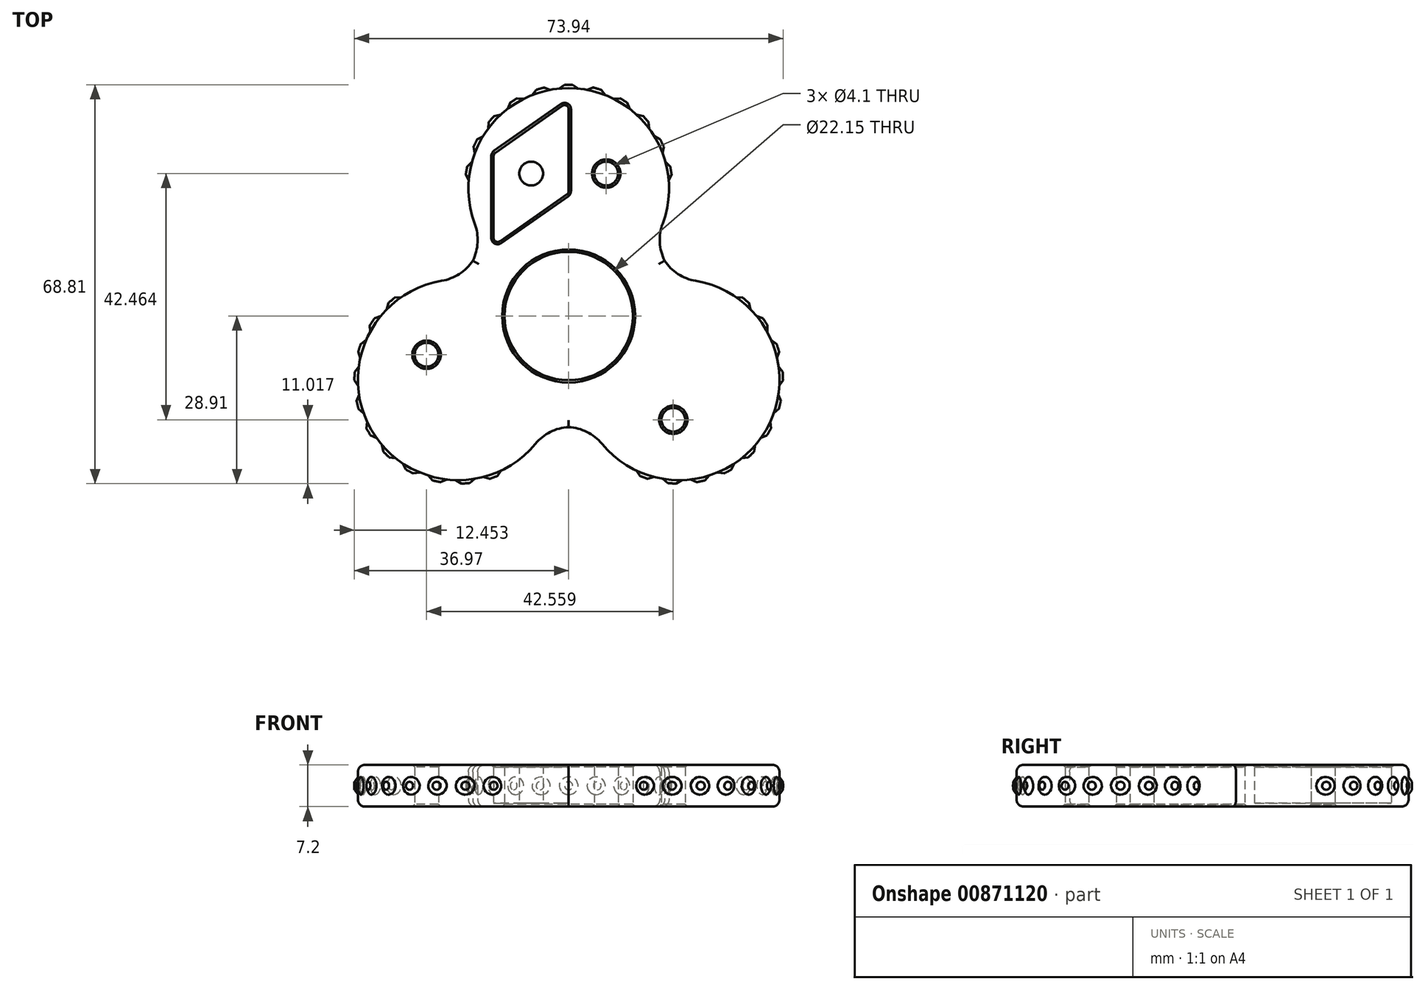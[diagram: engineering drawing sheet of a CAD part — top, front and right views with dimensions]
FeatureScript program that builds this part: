
annotation { "Feature Type Name" : "Feature", "Feature Type Description" : "" }
export const myFeature = defineFeature(function(context is Context, id is Id, definition is map)
    precondition{}
    {
        {
            var Q0;
            Q0=qCreatedBy(makeId("Top.planeOp"),FACE);
            var sketch = newSketch(context, id + "F0", { "sketchPlane" : qUnion([Q0])});
            skCircle(sketch, "E0", {"center": v(0, 0) * mm, "radius": 11.07 * mm});
            skCircle(sketch, "E1", {"center": v(0, 0) * mm, "radius": 26.5 * mm, "construction": true});
            skArc(sketch, "E2", {"start": v(-13.1, 23.03) * mm, "mid": v(-13.03, 22.75) * mm, "end": v(-12.95, 22.47) * mm, "construction": true});
            skLineSegment(sketch, "E3", {"start": v(0, 43.45) * mm, "end": v(0, 0) * mm});
            skLineSegment(sketch, "E4", {"start": v(0, 37) * mm, "end": v(12.95, 27.94) * mm});
            skLineSegment(sketch, "E5", {"start": v(12.95, 27.94) * mm, "end": v(12.95, 12.13) * mm});
            skLineSegment(sketch, "E6", {"start": v(12.95, 12.13) * mm, "end": v(0, 21.2) * mm});
            skLineSegment(sketch, "E7.MirrorCS", {"start": v(0, 37) * mm, "end": v(-12.95, 27.94) * mm});
            skLineSegment(sketch, "E8.MirrorCS", {"start": v(-12.95, 27.94) * mm, "end": v(-12.95, 12.13) * mm});
            skLineSegment(sketch, "E9.MirrorCS", {"start": v(-12.95, 12.13) * mm, "end": v(0, 21.2) * mm});
            skLineSegment(sketch, "E10.1.0", {"start": v(-32.1, -18.57) * mm, "end": v(-17.76, -25.25) * mm});
            skLineSegment(sketch, "E10.1.1", {"start": v(-17.76, -25.25) * mm, "end": v(-4.07, -17.35) * mm});
            skLineSegment(sketch, "E10.1.2", {"start": v(-4.07, -17.35) * mm, "end": v(-18.4, -10.67) * mm});
            skLineSegment(sketch, "E10.1.3", {"start": v(-17.02, 5.08) * mm, "end": v(-18.4, -10.67) * mm});
            skLineSegment(sketch, "E10.1.4", {"start": v(-30.71, -2.82) * mm, "end": v(-17.02, 5.08) * mm});
            skLineSegment(sketch, "E10.1.5", {"start": v(-32.1, -18.57) * mm, "end": v(-30.71, -2.82) * mm});
            skLineSegment(sketch, "E10.2.0", {"start": v(32.1, -18.57) * mm, "end": v(30.71, -2.82) * mm});
            skLineSegment(sketch, "E10.2.1", {"start": v(30.71, -2.82) * mm, "end": v(17.02, 5.08) * mm});
            skLineSegment(sketch, "E10.2.2", {"start": v(17.02, 5.08) * mm, "end": v(18.4, -10.67) * mm});
            skLineSegment(sketch, "E10.2.3", {"start": v(4.07, -17.35) * mm, "end": v(18.4, -10.67) * mm});
            skLineSegment(sketch, "E10.2.4", {"start": v(17.76, -25.25) * mm, "end": v(4.07, -17.35) * mm});
            skLineSegment(sketch, "E10.2.5", {"start": v(32.1, -18.57) * mm, "end": v(17.76, -25.25) * mm});
            skPoint(sketch, "E10.center", {"position": v(0, -0.05) * mm});
            skArc(sketch, "E11.trimOffspring", {"start": v(12.95, 22.47) * mm, "mid": v(13, 22.77) * mm, "end": v(13.05, 23.06) * mm, "construction": true});
            skCircle(sketch, "E12", {"center": v(0, 22) * mm, "radius": 17.3 * mm});
            skCircle(sketch, "E13.1.0", {"center": v(-19.05, -11) * mm, "radius": 17.3 * mm});
            skCircle(sketch, "E13.2.0", {"center": v(19.05, -11) * mm, "radius": 17.3 * mm});
            skLineSegment(sketch, "E14", {"start": v(-17.02, 5.08) * mm, "end": v(-12.95, 12.13) * mm});
            skLineSegment(sketch, "E15", {"start": v(12.95, 12.13) * mm, "end": v(17.02, 5.08) * mm});
            skLineSegment(sketch, "E16", {"start": v(4.07, -17.35) * mm, "end": v(-4.07, -17.35) * mm});
            skLineSegment(sketch, "E17", {"start": v(-7.18, -19.14) * mm, "end": v(7.18, -19.14) * mm});
            skLineSegment(sketch, "E18.1.0", {"start": v(20.13, 3.3) * mm, "end": v(12.96, 15.73) * mm});
            skLineSegment(sketch, "E18.2.0", {"start": v(-12.96, 15.73) * mm, "end": v(-20.13, 3.3) * mm});
            skPoint(sketch, "E18.center", {"position": v(0, -0.03) * mm});
            skLineSegment(sketch, "E19", {"start": v(-12.95, 27.94) * mm, "end": v(0, 21.2) * mm, "construction": true});
            skLineSegment(sketch, "E20", {"start": v(-12.95, 12.13) * mm, "end": v(0, 37) * mm, "construction": true});
            skCircle(sketch, "E21", {"center": v(-6.47, 24.57) * mm, "radius": 2.05 * mm});
            skCircle(sketch, "E22.MirrorC", {"center": v(6.47, 24.57) * mm, "radius": 2.05 * mm});
            skCircle(sketch, "E23.1.0", {"center": v(-24.52, -6.68) * mm, "radius": 2.05 * mm});
            skCircle(sketch, "E23.1.1", {"center": v(-18.04, -17.9) * mm, "radius": 2.05 * mm});
            skCircle(sketch, "E23.2.0", {"center": v(18.04, -17.9) * mm, "radius": 2.05 * mm});
            skCircle(sketch, "E23.2.1", {"center": v(24.52, -6.68) * mm, "radius": 2.05 * mm});
            skSolve(sketch);
        }
        {
            var Q0;
            {var subQ1=sQuery(id+"F0.wireOp",EDGE,"E7.MirrorCS");Q0=makeQuery(id+"F0.imprint","IMPRINT",FACE,{"disambiguationData":[TD([[makeQuery(id+"F0.imprint","IMPRINT",EDGE,{"derivedFrom":subQ1}),-1.0]])]});}
            var Q1;
            {var subQ0=sQuery(id+"F0.wireOp",EDGE,"E4");Q1=makeQuery(id+"F0.imprint","IMPRINT",FACE,{"disambiguationData":[TD([[makeQuery(id+"F0.imprint","IMPRINT",EDGE,{"derivedFrom":subQ0}),1.0]])]});}
            var Q2;
            {var subQ5=sQuery(id+"F0.wireOp",EDGE,"E6");Q2=makeQuery(id+"F0.imprint","IMPRINT",FACE,{"disambiguationData":[TD([[makeQuery(id+"F0.imprint","IMPRINT",EDGE,{"derivedFrom":subQ5}),1.0]])]});}
            var Q3;
            {var subQ0=sQuery(id+"F0.wireOp",EDGE,"E9.MirrorCS");Q3=makeQuery(id+"F0.imprint","IMPRINT",FACE,{"disambiguationData":[TD([[makeQuery(id+"F0.imprint","IMPRINT",EDGE,{"derivedFrom":subQ0}),-1.0]])]});}
            var Q4;
            {var subQ0=sQuery(id+"F0.wireOp",EDGE,"E12");var subQ1=sQuery(id+"F0.wireOp",EDGE,"E0");var subQ2=makeQuery(id+"F0.imprint","INTERSECT",VERTEX,{"disambiguationData":[OD(1.0)],"derivedFrom":[subQ1,subQ0]});Q4=makeQuery(id+"F0.imprint","IMPRINT",FACE,{"disambiguationData":[TD([[makeQuery(id+"F0.imprint","IMPRINT",EDGE,{"disambiguationData":[TD([[subQ2,-1.0]])],"derivedFrom":subQ1}),-1.0]])]});}
            var Q5;
            {var subQ1=sQuery(id+"F0.wireOp",EDGE,"E10.1.2");Q5=makeQuery(id+"F0.imprint","IMPRINT",FACE,{"disambiguationData":[TD([[makeQuery(id+"F0.imprint","IMPRINT",EDGE,{"derivedFrom":subQ1}),-1.0]])]});}
            var Q6;
            {var subQ0=sQuery(id+"F0.wireOp",EDGE,"E13.1.0");var subQ1=sQuery(id+"F0.wireOp",EDGE,"E0");var subQ2=makeQuery(id+"F0.imprint","INTERSECT",VERTEX,{"disambiguationData":[OD(1.0)],"derivedFrom":[subQ1,subQ0]});Q6=makeQuery(id+"F0.imprint","IMPRINT",FACE,{"disambiguationData":[TD([[makeQuery(id+"F0.imprint","IMPRINT",EDGE,{"disambiguationData":[TD([[subQ2,-1.0]])],"derivedFrom":subQ1}),-1.0]])]});}
            var Q7;
            {var subQ9=sQuery(id+"F0.wireOp",EDGE,"E10.2.2");Q7=makeQuery(id+"F0.imprint","IMPRINT",FACE,{"disambiguationData":[TD([[makeQuery(id+"F0.imprint","IMPRINT",EDGE,{"derivedFrom":subQ9}),-1.0]])]});}
            var Q8;
            {var subQ0=sQuery(id+"F0.wireOp",EDGE,"E12");var subQ1=sQuery(id+"F0.wireOp",EDGE,"E0");var subQ2=makeQuery(id+"F0.imprint","INTERSECT",VERTEX,{"disambiguationData":[OD(0.0)],"derivedFrom":[subQ1,subQ0]});Q8=makeQuery(id+"F0.imprint","IMPRINT",FACE,{"disambiguationData":[TD([[makeQuery(id+"F0.imprint","IMPRINT",EDGE,{"disambiguationData":[TD([[subQ2,1.0]])],"derivedFrom":subQ1}),-1.0]])]});}
            var Q9;
            {var subQ6=sQuery(id+"F0.wireOp",EDGE,"E10.2.0");Q9=makeQuery(id+"F0.imprint","IMPRINT",FACE,{"disambiguationData":[TD([[makeQuery(id+"F0.imprint","IMPRINT",EDGE,{"derivedFrom":subQ6}),-1.0]])]});}
            var Q10;
            {var subQ7=sQuery(id+"F0.wireOp",EDGE,"E10.1.0");Q10=makeQuery(id+"F0.imprint","IMPRINT",FACE,{"disambiguationData":[TD([[makeQuery(id+"F0.imprint","IMPRINT",EDGE,{"derivedFrom":subQ7}),-1.0]])]});}
            var Q11;
            {var subQ0=sQuery(id+"F0.wireOp",EDGE,"E18.2.0");var subQ1=sQuery(id+"F0.wireOp",EDGE,"E12");var subQ2=makeQuery(id+"F0.imprint","INTERSECT",VERTEX,{"derivedFrom":[subQ1,subQ0]});Q11=makeQuery(id+"F0.imprint","IMPRINT",FACE,{"disambiguationData":[TD([[makeQuery(id+"F0.imprint","IMPRINT",EDGE,{"disambiguationData":[TD([[subQ2,-1.0]])],"derivedFrom":subQ1}),-1.0]])]});}
            var Q12;
            {var subQ0=sQuery(id+"F0.wireOp",EDGE,"E17");var subQ1=sQuery(id+"F0.wireOp",EDGE,"E13.1.0");var subQ2=makeQuery(id+"F0.imprint","INTERSECT",VERTEX,{"derivedFrom":[subQ1,subQ0]});Q12=makeQuery(id+"F0.imprint","IMPRINT",FACE,{"disambiguationData":[TD([[makeQuery(id+"F0.imprint","IMPRINT",EDGE,{"disambiguationData":[TD([[subQ2,-1.0]])],"derivedFrom":subQ1}),-1.0]])]});}
            var Q13;
            {var subQ3=sQuery(id+"F0.wireOp",EDGE,"E18.2.0");var subQ5=sQuery(id+"F0.wireOp",EDGE,"E12");var subQ7=makeQuery(id+"F0.imprint","INTERSECT",VERTEX,{"derivedFrom":[subQ5,subQ3]});Q13=makeQuery(id+"F0.imprint","IMPRINT",FACE,{"disambiguationData":[TD([[makeQuery(id+"F0.imprint","IMPRINT",EDGE,{"disambiguationData":[TD([[subQ7,-1.0]])],"derivedFrom":subQ5}),1.0]])]});}
            var Q14;
            {var subQ3=sQuery(id+"F0.wireOp",EDGE,"E18.2.0");var subQ5=sQuery(id+"F0.wireOp",EDGE,"E13.1.0");var subQ7=makeQuery(id+"F0.imprint","INTERSECT",VERTEX,{"derivedFrom":[subQ5,subQ3]});Q14=makeQuery(id+"F0.imprint","IMPRINT",FACE,{"disambiguationData":[TD([[makeQuery(id+"F0.imprint","IMPRINT",EDGE,{"disambiguationData":[TD([[subQ7,1.0]])],"derivedFrom":subQ5}),1.0]])]});}
            var Q15;
            {var subQ3=sQuery(id+"F0.wireOp",EDGE,"E17");var subQ5=sQuery(id+"F0.wireOp",EDGE,"E13.1.0");var subQ6=makeQuery(id+"F0.imprint","INTERSECT",VERTEX,{"derivedFrom":[subQ5,subQ3]});Q15=makeQuery(id+"F0.imprint","IMPRINT",FACE,{"disambiguationData":[TD([[makeQuery(id+"F0.imprint","IMPRINT",EDGE,{"disambiguationData":[TD([[subQ6,-1.0]])],"derivedFrom":subQ5}),1.0]])]});}
            var Q16;
            {var subQ3=sQuery(id+"F0.wireOp",EDGE,"E17");var subQ5=sQuery(id+"F0.wireOp",EDGE,"E13.2.0");var subQ6=makeQuery(id+"F0.imprint","INTERSECT",VERTEX,{"derivedFrom":[subQ5,subQ3]});Q16=makeQuery(id+"F0.imprint","IMPRINT",FACE,{"disambiguationData":[TD([[makeQuery(id+"F0.imprint","IMPRINT",EDGE,{"disambiguationData":[TD([[subQ6,1.0]])],"derivedFrom":subQ5}),1.0]])]});}
            var Q17;
            {var subQ3=sQuery(id+"F0.wireOp",EDGE,"E18.1.0");var subQ5=sQuery(id+"F0.wireOp",EDGE,"E12");var subQ7=makeQuery(id+"F0.imprint","INTERSECT",VERTEX,{"derivedFrom":[subQ5,subQ3]});Q17=makeQuery(id+"F0.imprint","IMPRINT",FACE,{"disambiguationData":[TD([[makeQuery(id+"F0.imprint","IMPRINT",EDGE,{"disambiguationData":[TD([[subQ7,1.0]])],"derivedFrom":subQ5}),1.0]])]});}
            var Q18;
            {var subQ3=sQuery(id+"F0.wireOp",EDGE,"E18.1.0");var subQ5=sQuery(id+"F0.wireOp",EDGE,"E13.2.0");var subQ6=makeQuery(id+"F0.imprint","INTERSECT",VERTEX,{"derivedFrom":[subQ5,subQ3]});Q18=makeQuery(id+"F0.imprint","IMPRINT",FACE,{"disambiguationData":[TD([[makeQuery(id+"F0.imprint","IMPRINT",EDGE,{"disambiguationData":[TD([[subQ6,-1.0]])],"derivedFrom":subQ5}),1.0]])]});}
            var Q19;
            {var subQ0=sQuery(id+"F0.wireOp",EDGE,"E18.1.0");var subQ1=sQuery(id+"F0.wireOp",EDGE,"E12");var subQ2=makeQuery(id+"F0.imprint","INTERSECT",VERTEX,{"derivedFrom":[subQ1,subQ0]});Q19=makeQuery(id+"F0.imprint","IMPRINT",FACE,{"disambiguationData":[TD([[makeQuery(id+"F0.imprint","IMPRINT",EDGE,{"disambiguationData":[TD([[subQ2,1.0]])],"derivedFrom":subQ1}),-1.0]])]});}
            var Q20;
            Q20=makeQuery(id+"F0.imprint","IMPRINT",FACE,{"disambiguationData":[TD([[makeQuery(id+"F0.imprint","IMPRINT",EDGE,{"derivedFrom":sQuery(id+"F0.wireOp",EDGE,"E23.1.0")}),-1.0]])]});
            var Q21;
            Q21=makeQuery(id+"F0.imprint","IMPRINT",FACE,{"disambiguationData":[TD([[makeQuery(id+"F0.imprint","IMPRINT",EDGE,{"derivedFrom":sQuery(id+"F0.wireOp",EDGE,"E23.1.1")}),1.0]])]});
            var Q22;
            Q22=makeQuery(id+"F0.imprint","IMPRINT",FACE,{"disambiguationData":[TD([[makeQuery(id+"F0.imprint","IMPRINT",EDGE,{"derivedFrom":sQuery(id+"F0.wireOp",EDGE,"E23.2.1")}),1.0]])]});
            var Q23;
            Q23=makeQuery(id+"F0.imprint","IMPRINT",FACE,{"disambiguationData":[TD([[makeQuery(id+"F0.imprint","IMPRINT",EDGE,{"derivedFrom":sQuery(id+"F0.wireOp",EDGE,"E23.2.0")}),-1.0]])]});
            var Q24;
            Q24=makeQuery(id+"F0.imprint","IMPRINT",FACE,{"disambiguationData":[TD([[makeQuery(id+"F0.imprint","IMPRINT",EDGE,{"derivedFrom":sQuery(id+"F0.wireOp",EDGE,"E22.MirrorC")}),-1.0]])]});
            var Q25;
            Q25=makeQuery(id+"F0.imprint","IMPRINT",FACE,{"disambiguationData":[TD([[makeQuery(id+"F0.imprint","IMPRINT",EDGE,{"derivedFrom":sQuery(id+"F0.wireOp",EDGE,"E21")}),1.0]])]});
            extrude(context, id + "F1", {"entities" : qUnion([Q0, Q1, Q2, Q3, Q4, Q5, Q6, Q7, Q8, Q9, Q10, Q11, Q12, Q13, Q14, Q15, Q16, Q17, Q18, Q19, Q20, Q21, Q22, Q23, Q24, Q25]), "depth" : 7.2 * mm, "offsetDistance" : 25 * mm});
        }
        {
            var Q0;
            {var subQ1=sQuery(id+"F0.wireOp",EDGE,"E4");Q0=makeQuery(id+"F0.imprint","IMPRINT",FACE,{"disambiguationData":[TD([[makeQuery(id+"F0.imprint","IMPRINT",EDGE,{"derivedFrom":subQ1}),-1.0]])]});}
            var Q1;
            {var subQ3=sQuery(id+"F0.wireOp",EDGE,"E7.MirrorCS");Q1=makeQuery(id+"F0.imprint","IMPRINT",FACE,{"disambiguationData":[TD([[makeQuery(id+"F0.imprint","IMPRINT",EDGE,{"derivedFrom":subQ3}),1.0]])]});}
            var Q2;
            {var subQ3=sQuery(id+"F0.wireOp",EDGE,"E10.2.0");Q2=makeQuery(id+"F0.imprint","IMPRINT",FACE,{"disambiguationData":[TD([[makeQuery(id+"F0.imprint","IMPRINT",EDGE,{"derivedFrom":subQ3}),1.0]])]});}
            var Q3;
            {var subQ3=sQuery(id+"F0.wireOp",EDGE,"E10.1.0");Q3=makeQuery(id+"F0.imprint","IMPRINT",FACE,{"disambiguationData":[TD([[makeQuery(id+"F0.imprint","IMPRINT",EDGE,{"derivedFrom":subQ3}),1.0]])]});}
            extrude(context, id + "F2", {"entities" : qUnion([Q0, Q1, Q2, Q3]), "operationType" : NewBodyOperationType.ADD, "depth" : 0.6 * mm, "offsetDistance" : 25 * mm});
        }
        {
            var Q0;
            Q0=makeQuery(id+"F1.opExtrude","SWEPT_EDGE",EDGE,{"disambiguationData":[OSD([sQuery(id+"F0.wireOp",EDGE,"E12"),sQuery(id+"F0.wireOp",EDGE,"Zo6cloxw-RQWd-VoTV-Hmrh-WUM4IXPVoAln")])]});
            var Q1;
            Q1=makeQuery(id+"F1.opExtrude","SWEPT_EDGE",EDGE,{"disambiguationData":[OSD([sQuery(id+"F0.wireOp",EDGE,"E13.1.0"),sQuery(id+"F0.wireOp",EDGE,"Zo6cloxw-RQWd-VoTV-Hmrh-WUM4IXPVoAln")])]});
            var Q2;
            Q2=makeQuery(id+"F1.opExtrude","SWEPT_EDGE",EDGE,{"disambiguationData":[OSD([sQuery(id+"F0.wireOp",EDGE,"E13.2.0"),sQuery(id+"F0.wireOp",EDGE,"qCIH2ttQ-GXot-xXQ0-Qejf-B46ZgPa41a3F")])]});
            var Q3;
            Q3=makeQuery(id+"F1.opExtrude","SWEPT_EDGE",EDGE,{"disambiguationData":[OSD([sQuery(id+"F0.wireOp",EDGE,"E12"),sQuery(id+"F0.wireOp",EDGE,"qCIH2ttQ-GXot-xXQ0-Qejf-B46ZgPa41a3F")])]});
            var Q4;
            Q4=makeQuery(id+"F1.opExtrude","SWEPT_EDGE",EDGE,{"disambiguationData":[OSD([sQuery(id+"F0.wireOp",EDGE,"E13.2.0"),sQuery(id+"F0.wireOp",EDGE,"L0YcY93C-S2HS-15lv-KyWX-i7wwrRtpjOze")])]});
            var Q5;
            Q5=makeQuery(id+"F1.opExtrude","SWEPT_EDGE",EDGE,{"disambiguationData":[OSD([sQuery(id+"F0.wireOp",EDGE,"E13.1.0"),sQuery(id+"F0.wireOp",EDGE,"L0YcY93C-S2HS-15lv-KyWX-i7wwrRtpjOze")])]});
            fillet(context, id + "F3", {"entities" : qUnion([Q0, Q1, Q2, Q3, Q4, Q5]), "radius" : 8 * mm, "tangentPropagation" : true, "allowEdgeOverflow" : false});
        }
        {
            var Q0;
            Q0=makeQuery(id+"F1.opExtrude","CAP_EDGE",EDGE,{"disambiguationData":[OSD([sQuery(id+"F0.wireOp",EDGE,"E13.2.0")])],"isStart":true});
            var Q1;
            Q1=makeQuery(id+"F1.opExtrude","CAP_EDGE",EDGE,{"disambiguationData":[OSD([sQuery(id+"F0.wireOp",EDGE,"E13.1.0")])],"isStart":true});
            var Q2;
            Q2=makeQuery(id+"F1.opExtrude","CAP_EDGE",EDGE,{"disambiguationData":[OSD([sQuery(id+"F0.wireOp",EDGE,"E12")])],"isStart":true});
            var Q3;
            Q3=makeQuery(id+"F1.opExtrude","CAP_EDGE",EDGE,{"disambiguationData":[OSD([sQuery(id+"F0.wireOp",EDGE,"E12")])],"isStart":false});
            var Q4;
            Q4=makeQuery(id+"F1.opExtrude","CAP_EDGE",EDGE,{"disambiguationData":[OSD([sQuery(id+"F0.wireOp",EDGE,"E13.2.0")])],"isStart":false});
            var Q5;
            Q5=makeQuery(id+"F1.opExtrude","CAP_EDGE",EDGE,{"disambiguationData":[OSD([sQuery(id+"F0.wireOp",EDGE,"E13.1.0")])],"isStart":false});
            fillet(context, id + "F4", {"entities" : qUnion([Q0, Q1, Q2, Q3, Q4, Q5]), "radius" : 1.2 * mm, "tangentPropagation" : true, "allowEdgeOverflow" : false});
        }
        {
            var Q0;
            Q0=makeQuery(id+"F1.opExtrude","SWEPT_EDGE",EDGE,{"disambiguationData":[OSD([sQuery(id+"F0.wireOp",EDGE,"E10.1.0"),sQuery(id+"F0.wireOp",EDGE,"E10.1.5")])]});
            var Q1;
            Q1=makeQuery(id+"F1.opExtrude","SWEPT_EDGE",EDGE,{"disambiguationData":[OSD([sQuery(id+"F0.wireOp",EDGE,"E10.1.1"),sQuery(id+"F0.wireOp",EDGE,"E10.1.2"),sQuery(id+"F0.wireOp",EDGE,"L0YcY93C-S2HS-15lv-KyWX-i7wwrRtpjOze")])]});
            var Q2;
            Q2=makeQuery(id+"F1.opExtrude","SWEPT_EDGE",EDGE,{"disambiguationData":[OSD([sQuery(id+"F0.wireOp",EDGE,"E10.1.3"),sQuery(id+"F0.wireOp",EDGE,"E10.1.4"),sQuery(id+"F0.wireOp",EDGE,"Zo6cloxw-RQWd-VoTV-Hmrh-WUM4IXPVoAln")])]});
            var Q3;
            Q3=makeQuery(id+"F1.opExtrude","SWEPT_EDGE",EDGE,{"disambiguationData":[OSD([sQuery(id+"F0.wireOp",EDGE,"E10.1.0"),sQuery(id+"F0.wireOp",EDGE,"E10.1.1")])]});
            var Q4;
            Q4=makeQuery(id+"F1.opExtrude","SWEPT_EDGE",EDGE,{"disambiguationData":[OSD([sQuery(id+"F0.wireOp",EDGE,"E10.1.4"),sQuery(id+"F0.wireOp",EDGE,"E10.1.5")])]});
            var Q5;
            Q5=makeQuery(id+"F1.opExtrude","SWEPT_EDGE",EDGE,{"disambiguationData":[OSD([sQuery(id+"F0.wireOp",EDGE,"E10.2.3"),sQuery(id+"F0.wireOp",EDGE,"E10.2.4"),sQuery(id+"F0.wireOp",EDGE,"L0YcY93C-S2HS-15lv-KyWX-i7wwrRtpjOze")])]});
            var Q6;
            Q6=makeQuery(id+"F1.opExtrude","SWEPT_EDGE",EDGE,{"disambiguationData":[OSD([sQuery(id+"F0.wireOp",EDGE,"E10.2.4"),sQuery(id+"F0.wireOp",EDGE,"E10.2.5")])]});
            var Q7;
            Q7=makeQuery(id+"F1.opExtrude","SWEPT_EDGE",EDGE,{"disambiguationData":[OSD([sQuery(id+"F0.wireOp",EDGE,"E10.2.0"),sQuery(id+"F0.wireOp",EDGE,"E10.2.5")])]});
            var Q8;
            Q8=makeQuery(id+"F1.opExtrude","SWEPT_EDGE",EDGE,{"disambiguationData":[OSD([sQuery(id+"F0.wireOp",EDGE,"E10.2.0"),sQuery(id+"F0.wireOp",EDGE,"E10.2.1")])]});
            var Q9;
            Q9=makeQuery(id+"F1.opExtrude","SWEPT_EDGE",EDGE,{"disambiguationData":[OSD([sQuery(id+"F0.wireOp",EDGE,"E10.2.1"),sQuery(id+"F0.wireOp",EDGE,"E10.2.2"),sQuery(id+"F0.wireOp",EDGE,"qCIH2ttQ-GXot-xXQ0-Qejf-B46ZgPa41a3F")])]});
            var Q10;
            Q10=makeQuery(id+"F1.opExtrude","SWEPT_EDGE",EDGE,{"disambiguationData":[OSD([sQuery(id+"F0.wireOp",EDGE,"E5"),sQuery(id+"F0.wireOp",EDGE,"E6"),sQuery(id+"F0.wireOp",EDGE,"qCIH2ttQ-GXot-xXQ0-Qejf-B46ZgPa41a3F")])]});
            var Q11;
            Q11=makeQuery(id+"F1.opExtrude","SWEPT_EDGE",EDGE,{"disambiguationData":[OSD([sQuery(id+"F0.wireOp",EDGE,"E8.MirrorCS"),sQuery(id+"F0.wireOp",EDGE,"E9.MirrorCS"),sQuery(id+"F0.wireOp",EDGE,"Zo6cloxw-RQWd-VoTV-Hmrh-WUM4IXPVoAln")])]});
            var Q12;
            Q12=makeQuery(id+"F1.opExtrude","SWEPT_EDGE",EDGE,{"disambiguationData":[OSD([sQuery(id+"F0.wireOp",EDGE,"E4"),sQuery(id+"F0.wireOp",EDGE,"E5")])]});
            var Q13;
            Q13=makeQuery(id+"F1.opExtrude","SWEPT_EDGE",EDGE,{"disambiguationData":[OSD([sQuery(id+"F0.wireOp",EDGE,"E3"),sQuery(id+"F0.wireOp",EDGE,"E4"),sQuery(id+"F0.wireOp",EDGE,"E7.MirrorCS")])]});
            var Q14;
            Q14=makeQuery(id+"F1.opExtrude","SWEPT_EDGE",EDGE,{"disambiguationData":[OSD([sQuery(id+"F0.wireOp",EDGE,"E7.MirrorCS"),sQuery(id+"F0.wireOp",EDGE,"E8.MirrorCS")])]});
            fillet(context, id + "F5", {"entities" : qUnion([Q0, Q1, Q2, Q3, Q4, Q5, Q6, Q7, Q8, Q9, Q10, Q11, Q12, Q13, Q14]), "radius" : 0.7 * mm, "tangentPropagation" : true, "allowEdgeOverflow" : false});
        }
        {
            var Q0;
            Q0=makeQuery(id+"F1.opExtrude","CAP_FACE",FACE,{"disambiguationData":[OSD([sQuery(id+"F0.wireOp",EDGE,"E0"),sQuery(id+"F0.wireOp",EDGE,"E4"),sQuery(id+"F0.wireOp",EDGE,"E5"),sQuery(id+"F0.wireOp",EDGE,"E6"),sQuery(id+"F0.wireOp",EDGE,"E7.MirrorCS"),sQuery(id+"F0.wireOp",EDGE,"E8.MirrorCS"),sQuery(id+"F0.wireOp",EDGE,"E9.MirrorCS"),sQuery(id+"F0.wireOp",EDGE,"E10.1.0"),sQuery(id+"F0.wireOp",EDGE,"E10.1.1"),sQuery(id+"F0.wireOp",EDGE,"E10.1.2"),sQuery(id+"F0.wireOp",EDGE,"E10.1.3"),sQuery(id+"F0.wireOp",EDGE,"E10.1.4"),sQuery(id+"F0.wireOp",EDGE,"E10.1.5"),sQuery(id+"F0.wireOp",EDGE,"E10.2.0"),sQuery(id+"F0.wireOp",EDGE,"E10.2.1"),sQuery(id+"F0.wireOp",EDGE,"E10.2.2"),sQuery(id+"F0.wireOp",EDGE,"E10.2.3"),sQuery(id+"F0.wireOp",EDGE,"E10.2.4"),sQuery(id+"F0.wireOp",EDGE,"E10.2.5"),sQuery(id+"F0.wireOp",EDGE,"E12"),sQuery(id+"F0.wireOp",EDGE,"E13.1.0"),sQuery(id+"F0.wireOp",EDGE,"E13.2.0"),sQuery(id+"F0.wireOp",EDGE,"qCIH2ttQ-GXot-xXQ0-Qejf-B46ZgPa41a3F"),sQuery(id+"F0.wireOp",EDGE,"Zo6cloxw-RQWd-VoTV-Hmrh-WUM4IXPVoAln"),sQuery(id+"F0.wireOp",EDGE,"L0YcY93C-S2HS-15lv-KyWX-i7wwrRtpjOze")])],"isStart":true});
            var Q1;
            Q1=makeQuery(id+"F1.opExtrude","CAP_FACE",FACE,{"disambiguationData":[OSD([sQuery(id+"F0.wireOp",EDGE,"E0"),sQuery(id+"F0.wireOp",EDGE,"E4"),sQuery(id+"F0.wireOp",EDGE,"E5"),sQuery(id+"F0.wireOp",EDGE,"E6"),sQuery(id+"F0.wireOp",EDGE,"E7.MirrorCS"),sQuery(id+"F0.wireOp",EDGE,"E8.MirrorCS"),sQuery(id+"F0.wireOp",EDGE,"E9.MirrorCS"),sQuery(id+"F0.wireOp",EDGE,"E10.1.0"),sQuery(id+"F0.wireOp",EDGE,"E10.1.1"),sQuery(id+"F0.wireOp",EDGE,"E10.1.2"),sQuery(id+"F0.wireOp",EDGE,"E10.1.3"),sQuery(id+"F0.wireOp",EDGE,"E10.1.4"),sQuery(id+"F0.wireOp",EDGE,"E10.1.5"),sQuery(id+"F0.wireOp",EDGE,"E10.2.0"),sQuery(id+"F0.wireOp",EDGE,"E10.2.1"),sQuery(id+"F0.wireOp",EDGE,"E10.2.2"),sQuery(id+"F0.wireOp",EDGE,"E10.2.3"),sQuery(id+"F0.wireOp",EDGE,"E10.2.4"),sQuery(id+"F0.wireOp",EDGE,"E10.2.5"),sQuery(id+"F0.wireOp",EDGE,"E12"),sQuery(id+"F0.wireOp",EDGE,"E13.1.0"),sQuery(id+"F0.wireOp",EDGE,"E13.2.0"),sQuery(id+"F0.wireOp",EDGE,"qCIH2ttQ-GXot-xXQ0-Qejf-B46ZgPa41a3F"),sQuery(id+"F0.wireOp",EDGE,"Zo6cloxw-RQWd-VoTV-Hmrh-WUM4IXPVoAln"),sQuery(id+"F0.wireOp",EDGE,"L0YcY93C-S2HS-15lv-KyWX-i7wwrRtpjOze")])],"isStart":false});
            chamfer(context, id + "F6", {"entities" : qUnion([Q0, Q1]), "width" : 0.4 * mm, "tangentPropagation" : true});
        }
        {
            var Q0;
            {var subQ0=sQuery(id+"F0.wireOp",EDGE,"E12");Q0=makeQuery(id+"F4.opFillet","BLEND_EDGE",EDGE,{"blendedFrom":[makeQuery(id+"F1.opExtrude","CAP_EDGE",EDGE,{"disambiguationData":[OSD([subQ0])],"isStart":true}),makeQuery(id+"F1.opExtrude","SWEPT_FACE",FACE,{"disambiguationData":[OSD([subQ0])]})],"blendedInto":[makeQuery(id+"F1.opExtrude","SWEPT_FACE",FACE,{"disambiguationData":[OSD([subQ0])]})]});}
            cPoint(context, id + "F7", {"entities" : qUnion([Q0]), "parameter" : 0.5});
        }
        {
            var Q0;
            Q0=qCreatedBy(makeId("Front.planeOp"),FACE);
            var Q1;
            Q1=qCreatedBy(id+"F7",VERTEX);
            cPlane(context, id + "F8", {"entities" : qUnion([Q0, Q1]), "cplaneType" : CPlaneType.PLANE_POINT, "offset" : 25 * mm, "width" : 150 * mm, "height" : 150 * mm});
        }
        {
            var Q0;
            Q0=qCreatedBy(id+"F8.planeOp",FACE);
            var sketch = newSketch(context, id + "F9", { "sketchPlane" : qUnion([Q0])});
            skCircle(sketch, "E24", {"center": v(0, 3.6) * mm, "radius": 1.8 * mm});
            skSolve(sketch);
        }
        {
            var Q0;
            Q0=makeQuery(id+"F9.imprint","IMPRINT",FACE,{"disambiguationData":[TD([[makeQuery(id+"F9.imprint","IMPRINT",EDGE,{"derivedFrom":sQuery(id+"F9.wireOp",EDGE,"E24")}),1.0]])]});
            var Q1;
            Q1=sQuery(id+"F9.wireOp",EDGE,"E24");
            extrude(context, id + "F10", {"entities" : qUnion([Q0]), "surfaceEntities" : qUnion([Q1]), "oppositeDirection" : true, "depth" : 0.6 * mm, "offsetDistance" : 25 * mm, "hasSecondDirection" : true, "secondDirectionOppositeDirection" : false, "secondDirectionDepth" : 0.4 * mm});
        }
        {
            var Q0;
            Q0=makeQuery(id+"F10.opExtrude","CAP_EDGE",EDGE,{"disambiguationData":[OSD([sQuery(id+"F9.wireOp",EDGE,"E24")])],"isStart":false});
            chamfer(context, id + "F11", {"entities" : qUnion([Q0]), "chamferType" : ChamferType.TWO_OFFSETS, "width1" : 0.8 * mm, "oppositeDirection" : false, "width2" : 1.1 * mm, "tangentPropagation" : true});
        }
        {
            var Q0;
            Q0=makeQuery(id+"F10.opExtrude","SWEPT_BODY",BODY,{"disambiguationData":[OSD([sQuery(id+"F9.wireOp",EDGE,"E24")])]});
            var Q1;
            Q1=makeQuery(id+"F1.opExtrude","SWEPT_FACE",FACE,{"disambiguationData":[OSD([sQuery(id+"F0.wireOp",EDGE,"E12")])]});
            circularPattern(context, id + "F12", {"entities" : qUnion([Q0]), "axis" : qUnion([Q1]), "angle" : 80 * degree, "instanceCount" : 6, "equalSpace" : true, "isCentered" : true});
        }
        {
            var Q0;
            Q0=makeQuery(id+"F10.opExtrude","SWEPT_BODY",BODY,{"disambiguationData":[OSD([sQuery(id+"F9.wireOp",EDGE,"E24")])]});
            var Q1;
            Q1=makeQuery(id+"F12.opPattern","COPY",BODY,{"derivedFrom":makeQuery(id+"F10.opExtrude","SWEPT_BODY",BODY,{"disambiguationData":[OSD([sQuery(id+"F9.wireOp",EDGE,"E24")])]}),"instanceName":"-8"});
            var Q2;
            Q2=makeQuery(id+"F12.opPattern","COPY",BODY,{"derivedFrom":makeQuery(id+"F10.opExtrude","SWEPT_BODY",BODY,{"disambiguationData":[OSD([sQuery(id+"F9.wireOp",EDGE,"E24")])]}),"instanceName":"-7"});
            var Q3;
            Q3=makeQuery(id+"F12.opPattern","COPY",BODY,{"derivedFrom":makeQuery(id+"F10.opExtrude","SWEPT_BODY",BODY,{"disambiguationData":[OSD([sQuery(id+"F9.wireOp",EDGE,"E24")])]}),"instanceName":"-6"});
            var Q4;
            Q4=makeQuery(id+"F12.opPattern","COPY",BODY,{"derivedFrom":makeQuery(id+"F10.opExtrude","SWEPT_BODY",BODY,{"disambiguationData":[OSD([sQuery(id+"F9.wireOp",EDGE,"E24")])]}),"instanceName":"-5"});
            var Q5;
            Q5=makeQuery(id+"F12.opPattern","COPY",BODY,{"derivedFrom":makeQuery(id+"F10.opExtrude","SWEPT_BODY",BODY,{"disambiguationData":[OSD([sQuery(id+"F9.wireOp",EDGE,"E24")])]}),"instanceName":"-4"});
            var Q6;
            Q6=makeQuery(id+"F12.opPattern","COPY",BODY,{"derivedFrom":makeQuery(id+"F10.opExtrude","SWEPT_BODY",BODY,{"disambiguationData":[OSD([sQuery(id+"F9.wireOp",EDGE,"E24")])]}),"instanceName":"-3"});
            var Q7;
            Q7=makeQuery(id+"F12.opPattern","COPY",BODY,{"derivedFrom":makeQuery(id+"F10.opExtrude","SWEPT_BODY",BODY,{"disambiguationData":[OSD([sQuery(id+"F9.wireOp",EDGE,"E24")])]}),"instanceName":"-2"});
            var Q8;
            Q8=makeQuery(id+"F12.opPattern","COPY",BODY,{"derivedFrom":makeQuery(id+"F10.opExtrude","SWEPT_BODY",BODY,{"disambiguationData":[OSD([sQuery(id+"F9.wireOp",EDGE,"E24")])]}),"instanceName":"-1"});
            var Q9;
            Q9=makeQuery(id+"F12.opPattern","COPY",BODY,{"derivedFrom":makeQuery(id+"F10.opExtrude","SWEPT_BODY",BODY,{"disambiguationData":[OSD([sQuery(id+"F9.wireOp",EDGE,"E24")])]}),"instanceName":"1"});
            var Q10;
            Q10=makeQuery(id+"F12.opPattern","COPY",BODY,{"derivedFrom":makeQuery(id+"F10.opExtrude","SWEPT_BODY",BODY,{"disambiguationData":[OSD([sQuery(id+"F9.wireOp",EDGE,"E24")])]}),"instanceName":"2"});
            var Q11;
            Q11=makeQuery(id+"F12.opPattern","COPY",BODY,{"derivedFrom":makeQuery(id+"F10.opExtrude","SWEPT_BODY",BODY,{"disambiguationData":[OSD([sQuery(id+"F9.wireOp",EDGE,"E24")])]}),"instanceName":"3"});
            var Q12;
            Q12=makeQuery(id+"F12.opPattern","COPY",BODY,{"derivedFrom":makeQuery(id+"F10.opExtrude","SWEPT_BODY",BODY,{"disambiguationData":[OSD([sQuery(id+"F9.wireOp",EDGE,"E24")])]}),"instanceName":"4"});
            var Q13;
            Q13=makeQuery(id+"F12.opPattern","COPY",BODY,{"derivedFrom":makeQuery(id+"F10.opExtrude","SWEPT_BODY",BODY,{"disambiguationData":[OSD([sQuery(id+"F9.wireOp",EDGE,"E24")])]}),"instanceName":"5"});
            var Q14;
            Q14=makeQuery(id+"F12.opPattern","COPY",BODY,{"derivedFrom":makeQuery(id+"F10.opExtrude","SWEPT_BODY",BODY,{"disambiguationData":[OSD([sQuery(id+"F9.wireOp",EDGE,"E24")])]}),"instanceName":"6"});
            var Q15;
            Q15=makeQuery(id+"F12.opPattern","COPY",BODY,{"derivedFrom":makeQuery(id+"F10.opExtrude","SWEPT_BODY",BODY,{"disambiguationData":[OSD([sQuery(id+"F9.wireOp",EDGE,"E24")])]}),"instanceName":"7"});
            var Q16;
            Q16=makeQuery(id+"F12.opPattern","COPY",BODY,{"derivedFrom":makeQuery(id+"F10.opExtrude","SWEPT_BODY",BODY,{"disambiguationData":[OSD([sQuery(id+"F9.wireOp",EDGE,"E24")])]}),"instanceName":"8"});
            var Q17;
            Q17=makeQuery(id+"F1.opExtrude","SWEPT_FACE",FACE,{"disambiguationData":[OSD([sQuery(id+"F0.wireOp",EDGE,"E0")])]});
            circularPattern(context, id + "F13", {"operationType" : NewBodyOperationType.ADD, "entities" : qUnion([Q0, Q1, Q2, Q3, Q4, Q5, Q6, Q7, Q8, Q9, Q10, Q11, Q12, Q13, Q14, Q15, Q16]), "axis" : qUnion([Q17]), "angle" : 360 * degree, "instanceCount" : 3, "equalSpace" : true});
        }
    });
